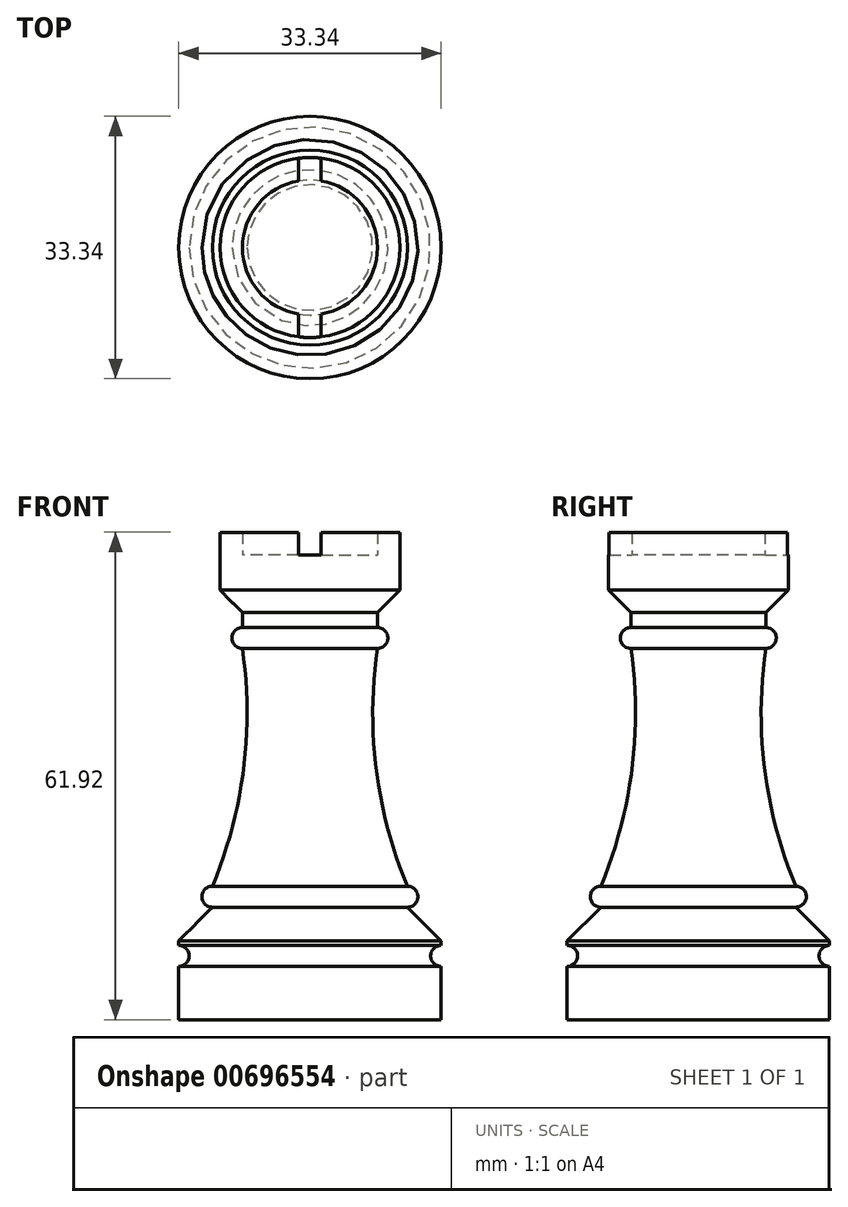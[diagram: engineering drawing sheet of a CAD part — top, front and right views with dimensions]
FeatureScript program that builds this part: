
annotation { "Feature Type Name" : "Feature", "Feature Type Description" : "" }
export const myFeature = defineFeature(function(context is Context, id is Id, definition is map)
    precondition{}
    {
        {
            var Q0;
            Q0=qCreatedBy(makeId("Front.planeOp"),FACE);
            var sketch = newSketch(context, id + "F0", { "sketchPlane" : qUnion([Q0])});
            skLineSegment(sketch, "E0", {"start": v(0, 0) * mm, "end": v(16.51, 0) * mm});
            skLineSegment(sketch, "E1", {"start": v(16.51, 0) * mm, "end": v(22.23, -5.71) * mm});
            skLineSegment(sketch, "E2", {"start": v(22.22, -5.71) * mm, "end": v(22.22, -6.48) * mm});
            skArc(sketch, "E3", {"start": v(22.22, -6.48) * mm, "mid": v(20.45, -8.25) * mm, "end": v(22.23, -10.03) * mm});
            skLineSegment(sketch, "E4", {"start": v(22.23, -10.03) * mm, "end": v(22.23, -19.05) * mm});
            skLineSegment(sketch, "E5", {"start": v(22.23, -19.05) * mm, "end": v(0, -19.05) * mm});
            skLineSegment(sketch, "E6", {"start": v(0, -19.05) * mm, "end": v(0, 0) * mm});
            skSolve(sketch);
        }
        {
            var Q0;
            Q0=makeQuery(id+"F0.imprint","IMPRINT",FACE,{"disambiguationData":[TD([[makeQuery(id+"F0.imprint","IMPRINT",EDGE,{"derivedFrom":sQuery(id+"F0.wireOp",EDGE,"E0")}),-1.0]])]});
            var Q1;
            Q1=sQuery(id+"F0.wireOp",EDGE,"E6");
            revolve(context, id + "F1", {"entities" : qUnion([Q0]), "axis" : qUnion([Q1]), "revolveType" : RevolveType.FULL});
        }
        {
            var Q0;
            Q0=qCreatedBy(makeId("Front.planeOp"),FACE);
            var sketch = newSketch(context, id + "F2", { "sketchPlane" : qUnion([Q0])});
            skLineSegment(sketch, "E7", {"start": v(0, 0) * mm, "end": v(0, 59.7) * mm});
            skLineSegment(sketch, "E8", {"start": v(0, 59.7) * mm, "end": v(11.43, 59.7) * mm});
            skLineSegment(sketch, "E9", {"start": v(11.43, 59.7) * mm, "end": v(11.43, 63.5) * mm});
            skLineSegment(sketch, "E10", {"start": v(11.43, 63.5) * mm, "end": v(15.24, 63.5) * mm});
            skLineSegment(sketch, "E11", {"start": v(15.24, 63.5) * mm, "end": v(15.24, 53.72) * mm});
            skLineSegment(sketch, "E12", {"start": v(15.24, 53.72) * mm, "end": v(11.43, 49.91) * mm});
            skLineSegment(sketch, "E13", {"start": v(11.43, 49.91) * mm, "end": v(11.43, 47.37) * mm});
            skArc(sketch, "E14", {"start": v(11.43, 43.81) * mm, "mid": v(13.2, 45.6) * mm, "end": v(11.43, 47.37) * mm});
            skArc(sketch, "E15", {"start": v(11.43, 43.81) * mm, "mid": v(11.24, 23.34) * mm, "end": v(16.5, 3.56) * mm});
            skArc(sketch, "E16", {"start": v(16.51, 0) * mm, "mid": v(18.29, 1.78) * mm, "end": v(16.51, 3.56) * mm});
            skLineSegment(sketch, "E17", {"start": v(16.51, 0) * mm, "end": v(0, 0) * mm});
            skSolve(sketch);
        }
        {
            var Q0;
            Q0=qSketchRegion(id+"F2",true);
            var Q1;
            Q1=sQuery(id+"F2.wireOp",EDGE,"E7");
            revolve(context, id + "F3", {"operationType" : NewBodyOperationType.ADD, "entities" : qUnion([Q0]), "axis" : qUnion([Q1]), "revolveType" : RevolveType.FULL});
        }
        {
            var Q0;
            Q0=qCreatedBy(makeId("Front.planeOp"),FACE);
            var sketch = newSketch(context, id + "F4", { "sketchPlane" : qUnion([Q0])});
            skLineSegment(sketch, "E18.bottom", {"start": v(1.9, 59.7) * mm, "end": v(-1.9, 59.7) * mm});
            skLineSegment(sketch, "E18.top", {"start": v(1.9, 63.5) * mm, "end": v(-1.9, 63.5) * mm});
            skLineSegment(sketch, "E18.left", {"start": v(1.9, 59.7) * mm, "end": v(1.9, 63.5) * mm});
            skLineSegment(sketch, "E18.right", {"start": v(-1.9, 59.7) * mm, "end": v(-1.9, 63.5) * mm});
            skPoint(sketch, "E18.middle", {"position": v(0, 61.6) * mm});
            skSolve(sketch);
        }
        {
            var Q0;
            Q0=qSketchRegion(id+"F4",true);
            extrude(context, id + "F5", {"entities" : qUnion([Q0]), "operationType" : NewBodyOperationType.REMOVE, "endBound" : BoundingType.THROUGH_ALL, "depth" : 25.4 * mm, "offsetDistance" : 25.4 * mm, "hasSecondDirection" : true, "secondDirectionBound" : SecondDirectionBoundingType.THROUGH_ALL, "secondDirectionOppositeDirection" : true, "secondDirectionDepth" : 25.4 * mm});
        }
        {
            var Q0;
            Q0=makeQuery(id+"F1.opRevolve","SWEPT_BODY",BODY,{"disambiguationData":[OSD([sQuery(id+"F0.wireOp",EDGE,"E0"),sQuery(id+"F0.wireOp",EDGE,"E1"),sQuery(id+"F0.wireOp",EDGE,"E2"),sQuery(id+"F0.wireOp",EDGE,"E3"),sQuery(id+"F0.wireOp",EDGE,"E4"),sQuery(id+"F0.wireOp",EDGE,"E5"),sQuery(id+"F0.wireOp",EDGE,"E6")])]});
            var Q1;
            Q1=sQuery(id+"F0.wireOp",VERTEX,"E6.end");
            transform(context, id + "F6", {"entities" : qUnion([Q0]), "transformType" : TransformType.SCALE_UNIFORMLY, "scale" : .75, "scalePoint" : qUnion([Q1]), "makeCopy" : false});
        }
    });
